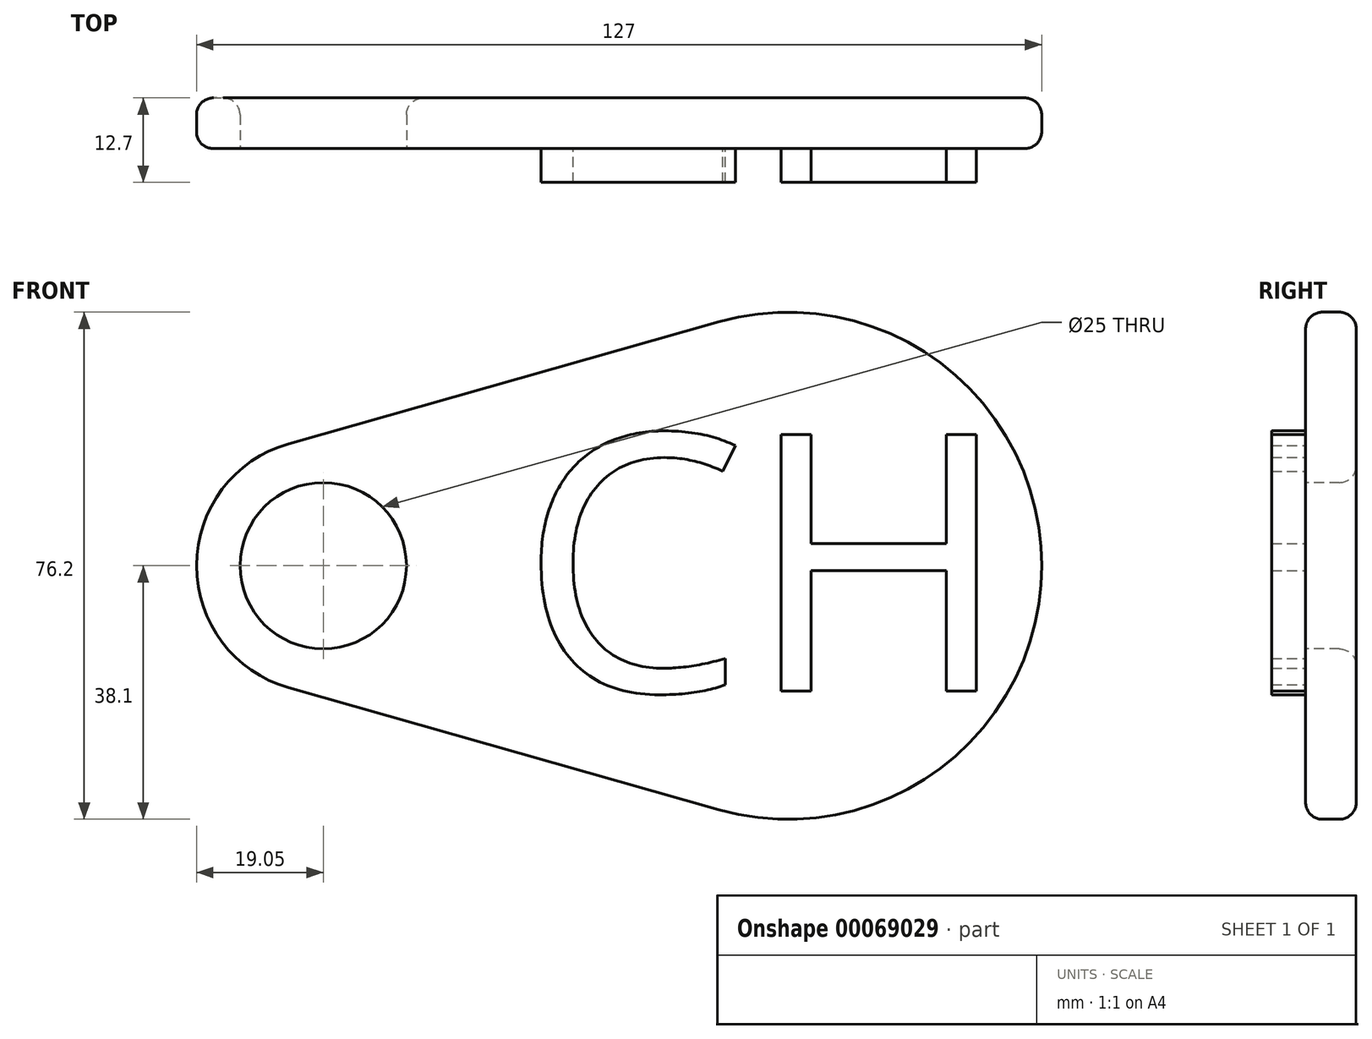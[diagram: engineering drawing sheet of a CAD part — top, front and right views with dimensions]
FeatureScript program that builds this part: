
annotation { "Feature Type Name" : "Feature", "Feature Type Description" : "" }
export const myFeature = defineFeature(function(context is Context, id is Id, definition is map)
    precondition{}
    {
        {
            var Q0;
            Q0=qCreatedBy(makeId("Front.planeOp"),FACE);
            var sketch = newSketch(context, id + "F0", { "sketchPlane" : qUnion([Q0])});
            skCircle(sketch, "E0", {"center": v(-69.85, 0) * mm, "radius": 19.05 * mm});
            skCircle(sketch, "E1", {"center": v(0, 0) * mm, "radius": 38.1 * mm});
            skLineSegment(sketch, "E2", {"start": v(-75.05, -18.33) * mm, "end": v(-10.4, -36.66) * mm});
            skLineSegment(sketch, "E3", {"start": v(-75.05, 18.33) * mm, "end": v(-10.4, 36.66) * mm});
            skSolve(sketch);
        }
        {
            var Q0;
            {var subQ0=sQuery(id+"F0.wireOp",EDGE,"E0");var subQ1=makeQuery(id+"F0.imprint","INTERSECT",VERTEX,{"derivedFrom":[subQ0,sQuery(id+"F0.wireOp",EDGE,"E2")]});Q0=makeQuery(id+"F0.imprint","IMPRINT",FACE,{"disambiguationData":[TD([[makeQuery(id+"F0.imprint","IMPRINT",EDGE,{"disambiguationData":[TD([[subQ1,1.0]])],"derivedFrom":subQ0}),1.0]])]});}
            var Q1;
            {var subQ0=sQuery(id+"F0.wireOp",EDGE,"E2");Q1=makeQuery(id+"F0.imprint","IMPRINT",FACE,{"disambiguationData":[TD([[makeQuery(id+"F0.imprint","IMPRINT",EDGE,{"derivedFrom":subQ0}),1.0]])]});}
            var Q2;
            {var subQ0=sQuery(id+"F0.wireOp",EDGE,"E1");var subQ1=makeQuery(id+"F0.imprint","INTERSECT",VERTEX,{"derivedFrom":[subQ0,sQuery(id+"F0.wireOp",EDGE,"E2")]});Q2=makeQuery(id+"F0.imprint","IMPRINT",FACE,{"disambiguationData":[TD([[makeQuery(id+"F0.imprint","IMPRINT",EDGE,{"disambiguationData":[TD([[subQ1,1.0]])],"derivedFrom":subQ0}),1.0]])]});}
            extrude(context, id + "F1", {"entities" : qUnion([Q0, Q1, Q2]), "depth" : 7.62 * mm});
        }
        {
            var Q0;
            Q0=makeQuery(id+"F1.opExtrude","CAP_FACE",FACE,{"disambiguationData":[OSD([sQuery(id+"F0.wireOp",EDGE,"E0"),sQuery(id+"F0.wireOp",EDGE,"E1"),sQuery(id+"F0.wireOp",EDGE,"E2"),sQuery(id+"F0.wireOp",EDGE,"E3")])],"isStart":false});
            var sketch = newSketch(context, id + "F2", { "sketchPlane" : qUnion([Q0])});
            skCircle(sketch, "E4", {"center": v(-69.85, 0) * mm, "radius": 12.5 * mm});
            skSolve(sketch);
        }
        {
            var Q0;
            Q0=makeQuery(id+"F2.imprint","IMPRINT",FACE,{"disambiguationData":[TD([[makeQuery(id+"F2.imprint","IMPRINT",EDGE,{"derivedFrom":sQuery(id+"F2.wireOp",EDGE,"E4")}),1.0]])]});
            extrude(context, id + "F3", {"entities" : qUnion([Q0]), "operationType" : NewBodyOperationType.REMOVE, "endBound" : BoundingType.THROUGH_ALL, "oppositeDirection" : true, "depth" : 25.4 * mm});
        }
        {
            var Q0;
            Q0=makeQuery(id+"F1.opExtrude","CAP_FACE",FACE,{"disambiguationData":[OSD([sQuery(id+"F0.wireOp",EDGE,"E0"),sQuery(id+"F0.wireOp",EDGE,"E1"),sQuery(id+"F0.wireOp",EDGE,"E2"),sQuery(id+"F0.wireOp",EDGE,"E3")])],"isStart":false});
            var sketch = newSketch(context, id + "F4", { "sketchPlane" : qUnion([Q0])});
            skText(sketch, "E5", { "text": "CH", "fontName": "OpenSans-Regular.ttf"});
            const initialGuessF4  = {"E5": [-0.04042, -0.01886, 1, 0, 0.0389]};
            skSetInitialGuess(sketch, initialGuessF4);
            skSolve(sketch);
        }
        {
            var Q0;
            Q0=makeQuery(id+"F4.imprint","IMPRINT",FACE,{"disambiguationData":[TD([[makeQuery(id+"F4.imprint","IMPRINT",EDGE,{"derivedFrom":sQuery(id+"F4.wireOp",EDGE,"E5.sketch_text.stroke-0")}),-1.0]])]});
            var Q1;
            Q1=makeQuery(id+"F4.imprint","IMPRINT",FACE,{"disambiguationData":[TD([[makeQuery(id+"F4.imprint","IMPRINT",EDGE,{"derivedFrom":sQuery(id+"F4.wireOp",EDGE,"E5.sketch_text.stroke-15")}),-1.0]])]});
            extrude(context, id + "F5", {"entities" : qUnion([Q0, Q1]), "operationType" : NewBodyOperationType.ADD, "depth" : 5.08 * mm});
        }
        {
            var Q0;
            Q0=makeQuery(id+"F1.opExtrude","CAP_EDGE",EDGE,{"disambiguationData":[OSD([sQuery(id+"F0.wireOp",EDGE,"E0")])],"isStart":false});
            var Q1;
            Q1=makeQuery(id+"F1.opExtrude","CAP_EDGE",EDGE,{"disambiguationData":[OSD([sQuery(id+"F0.wireOp",EDGE,"E3")])],"isStart":false});
            var Q2;
            Q2=makeQuery(id+"F1.opExtrude","CAP_EDGE",EDGE,{"disambiguationData":[OSD([sQuery(id+"F0.wireOp",EDGE,"E2")])],"isStart":false});
            var Q3;
            Q3=makeQuery(id+"F1.opExtrude","CAP_EDGE",EDGE,{"disambiguationData":[OSD([sQuery(id+"F0.wireOp",EDGE,"E1")])],"isStart":false});
            var Q4;
            Q4=makeQuery(id+"F3.boolean.opBoolean","COPY",EDGE,{"derivedFrom":makeQuery(id+"F3.opExtrude","CAP_EDGE",EDGE,{"disambiguationData":[OSD([sQuery(id+"F2.wireOp",EDGE,"E4")])],"isStart":true})});
            var Q5;
            Q5=makeQuery(id+"F1.opExtrude","CAP_EDGE",EDGE,{"disambiguationData":[OSD([sQuery(id+"F0.wireOp",EDGE,"E1")])],"isStart":true});
            var Q6;
            Q6=makeQuery(id+"F1.opExtrude","CAP_EDGE",EDGE,{"disambiguationData":[OSD([sQuery(id+"F0.wireOp",EDGE,"E3")])],"isStart":true});
            var Q7;
            Q7=makeQuery(id+"F1.opExtrude","CAP_EDGE",EDGE,{"disambiguationData":[OSD([sQuery(id+"F0.wireOp",EDGE,"E2")])],"isStart":true});
            var Q8;
            Q8=makeQuery(id+"F1.opExtrude","CAP_EDGE",EDGE,{"disambiguationData":[OSD([sQuery(id+"F0.wireOp",EDGE,"E0")])],"isStart":true});
            var Q9;
            Q9=makeQuery(id+"F3.boolean.opBoolean","INTERSECT",EDGE,{"derivedFrom":[makeQuery(id+"F1.opExtrude","CAP_FACE",FACE,{"disambiguationData":[OSD([sQuery(id+"F0.wireOp",EDGE,"E0"),sQuery(id+"F0.wireOp",EDGE,"E1"),sQuery(id+"F0.wireOp",EDGE,"E2"),sQuery(id+"F0.wireOp",EDGE,"E3")])],"isStart":true}),makeQuery(id+"F3.opExtrude","SWEPT_FACE",FACE,{"disambiguationData":[OSD([sQuery(id+"F2.wireOp",EDGE,"E4")])]})]});
            fillet(context, id + "F6", {"entities" : qUnion([Q0, Q1, Q2, Q3, Q4, Q5, Q6, Q7, Q8, Q9]), "radius" : 2.54 * mm, "tangentPropagation" : true, "allowEdgeOverflow" : false});
        }
    });
